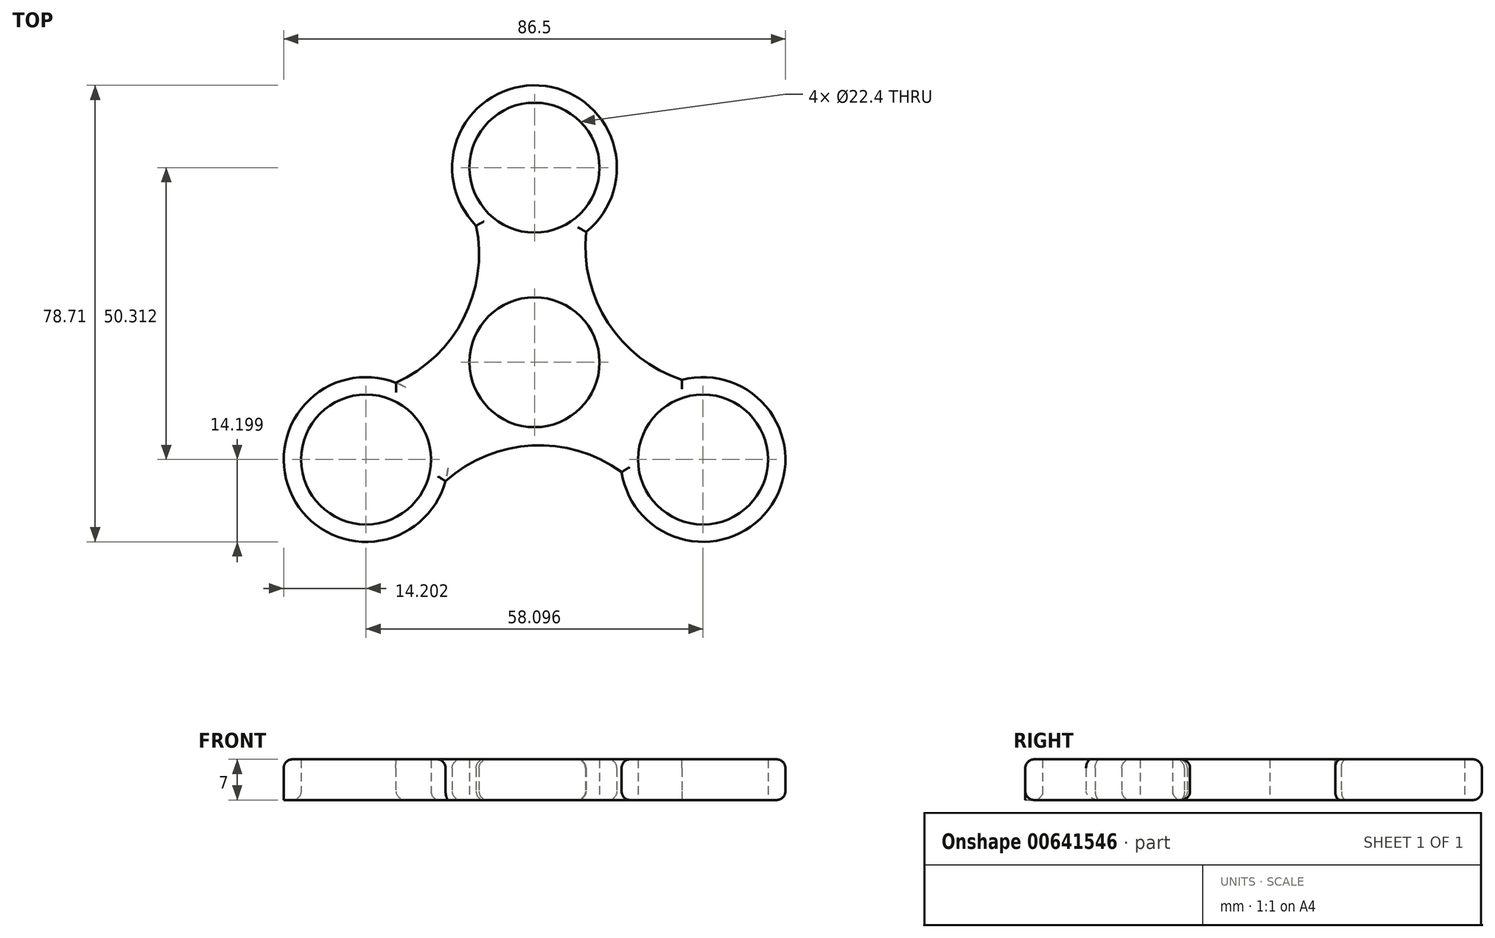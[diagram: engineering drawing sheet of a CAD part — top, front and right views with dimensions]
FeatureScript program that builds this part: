
annotation { "Feature Type Name" : "Feature", "Feature Type Description" : "" }
export const myFeature = defineFeature(function(context is Context, id is Id, definition is map)
    precondition{}
    {
        {
            var Q0;
            Q0=qCreatedBy(makeId("Top.planeOp"),FACE);
            var sketch = newSketch(context, id + "F0", { "sketchPlane" : qUnion([Q0])});
            skCircle(sketch, "E0", {"center": v(0, 0) * mm, "radius": 11.2 * mm});
            skCircle(sketch, "E1", {"center": v(0, 33.54) * mm, "radius": 11.2 * mm});
            skCircle(sketch, "E2", {"center": v(0, 33.54) * mm, "radius": 14.2 * mm});
            skCircle(sketch, "E3.1.0", {"center": v(-29.05, -16.77) * mm, "radius": 14.2 * mm});
            skCircle(sketch, "E3.1.1", {"center": v(-29.05, -16.77) * mm, "radius": 11.2 * mm});
            skCircle(sketch, "E3.2.0", {"center": v(29.05, -16.77) * mm, "radius": 14.2 * mm});
            skCircle(sketch, "E3.2.1", {"center": v(29.05, -16.77) * mm, "radius": 11.2 * mm});
            skArc(sketch, "E4", {"start": v(-23.9, -3.54) * mm, "mid": v(-12.23, 7.57) * mm, "end": v(-10.07, 23.53) * mm});
            skArc(sketch, "E5.1.0", {"start": v(15.01, -18.93) * mm, "mid": v(-0.44, -14.38) * mm, "end": v(-15.34, -20.48) * mm});
            skArc(sketch, "E5.2.0", {"start": v(8.88, 22.46) * mm, "mid": v(12.67, 6.8) * mm, "end": v(25.41, -3.04) * mm});
            skSolve(sketch);
        }
        {
            var Q0;
            Q0=makeQuery(id+"F0.imprint","IMPRINT",FACE,{"disambiguationData":[TD([[makeQuery(id+"F0.imprint","IMPRINT",EDGE,{"derivedFrom":sQuery(id+"F0.wireOp",EDGE,"E1")}),-1.0]])]});
            var Q1;
            Q1=makeQuery(id+"F0.imprint","IMPRINT",FACE,{"disambiguationData":[TD([[makeQuery(id+"F0.imprint","IMPRINT",EDGE,{"derivedFrom":sQuery(id+"F0.wireOp",EDGE,"E0")}),-1.0]])]});
            var Q2;
            Q2=makeQuery(id+"F0.imprint","IMPRINT",FACE,{"disambiguationData":[TD([[makeQuery(id+"F0.imprint","IMPRINT",EDGE,{"derivedFrom":sQuery(id+"F0.wireOp",EDGE,"E3.1.1")}),-1.0]])]});
            var Q3;
            Q3=makeQuery(id+"F0.imprint","IMPRINT",FACE,{"disambiguationData":[TD([[makeQuery(id+"F0.imprint","IMPRINT",EDGE,{"derivedFrom":sQuery(id+"F0.wireOp",EDGE,"E3.2.1")}),-1.0]])]});
            extrude(context, id + "F1", {"entities" : qUnion([Q0, Q1, Q2, Q3]), "depth" : 7 * mm, "offsetDistance" : 25 * mm});
        }
        {
            var Q0;
            Q0=makeQuery(id+"F1.opExtrude","CAP_EDGE",EDGE,{"disambiguationData":[OSD([sQuery(id+"F0.wireOp",EDGE,"E2")])],"isStart":false});
            var Q1;
            Q1=makeQuery(id+"F1.opExtrude","CAP_EDGE",EDGE,{"disambiguationData":[OSD([sQuery(id+"F0.wireOp",EDGE,"E4")])],"isStart":false});
            var Q2;
            Q2=makeQuery(id+"F1.opExtrude","CAP_EDGE",EDGE,{"disambiguationData":[OSD([sQuery(id+"F0.wireOp",EDGE,"E3.1.0")])],"isStart":false});
            var Q3;
            Q3=makeQuery(id+"F1.opExtrude","CAP_EDGE",EDGE,{"disambiguationData":[OSD([sQuery(id+"F0.wireOp",EDGE,"E5.1.0")])],"isStart":false});
            var Q4;
            Q4=makeQuery(id+"F1.opExtrude","CAP_EDGE",EDGE,{"disambiguationData":[OSD([sQuery(id+"F0.wireOp",EDGE,"E3.2.0")])],"isStart":false});
            var Q5;
            Q5=makeQuery(id+"F1.opExtrude","CAP_EDGE",EDGE,{"disambiguationData":[OSD([sQuery(id+"F0.wireOp",EDGE,"E5.2.0")])],"isStart":false});
            var Q6;
            Q6=makeQuery(id+"F1.opExtrude","CAP_EDGE",EDGE,{"disambiguationData":[OSD([sQuery(id+"F0.wireOp",EDGE,"E5.1.0")])],"isStart":true});
            var Q7;
            Q7=makeQuery(id+"F1.opExtrude","CAP_EDGE",EDGE,{"disambiguationData":[OSD([sQuery(id+"F0.wireOp",EDGE,"E3.1.1")])],"isStart":true});
            var Q8;
            Q8=makeQuery(id+"F1.opExtrude","CAP_EDGE",EDGE,{"disambiguationData":[OSD([sQuery(id+"F0.wireOp",EDGE,"E4")])],"isStart":true});
            var Q9;
            Q9=makeQuery(id+"F1.opExtrude","CAP_EDGE",EDGE,{"disambiguationData":[OSD([sQuery(id+"F0.wireOp",EDGE,"E2")])],"isStart":true});
            var Q10;
            Q10=makeQuery(id+"F1.opExtrude","CAP_EDGE",EDGE,{"disambiguationData":[OSD([sQuery(id+"F0.wireOp",EDGE,"E5.2.0")])],"isStart":true});
            var Q11;
            Q11=makeQuery(id+"F1.opExtrude","CAP_EDGE",EDGE,{"disambiguationData":[OSD([sQuery(id+"F0.wireOp",EDGE,"E3.2.0")])],"isStart":true});
            fillet(context, id + "F2", {"entities" : qUnion([Q0, Q1, Q2, Q3, Q4, Q5, Q6, Q7, Q8, Q9, Q10, Q11]), "radius" : 1.5 * mm, "tangentPropagation" : true, "allowEdgeOverflow" : false});
        }
    });
